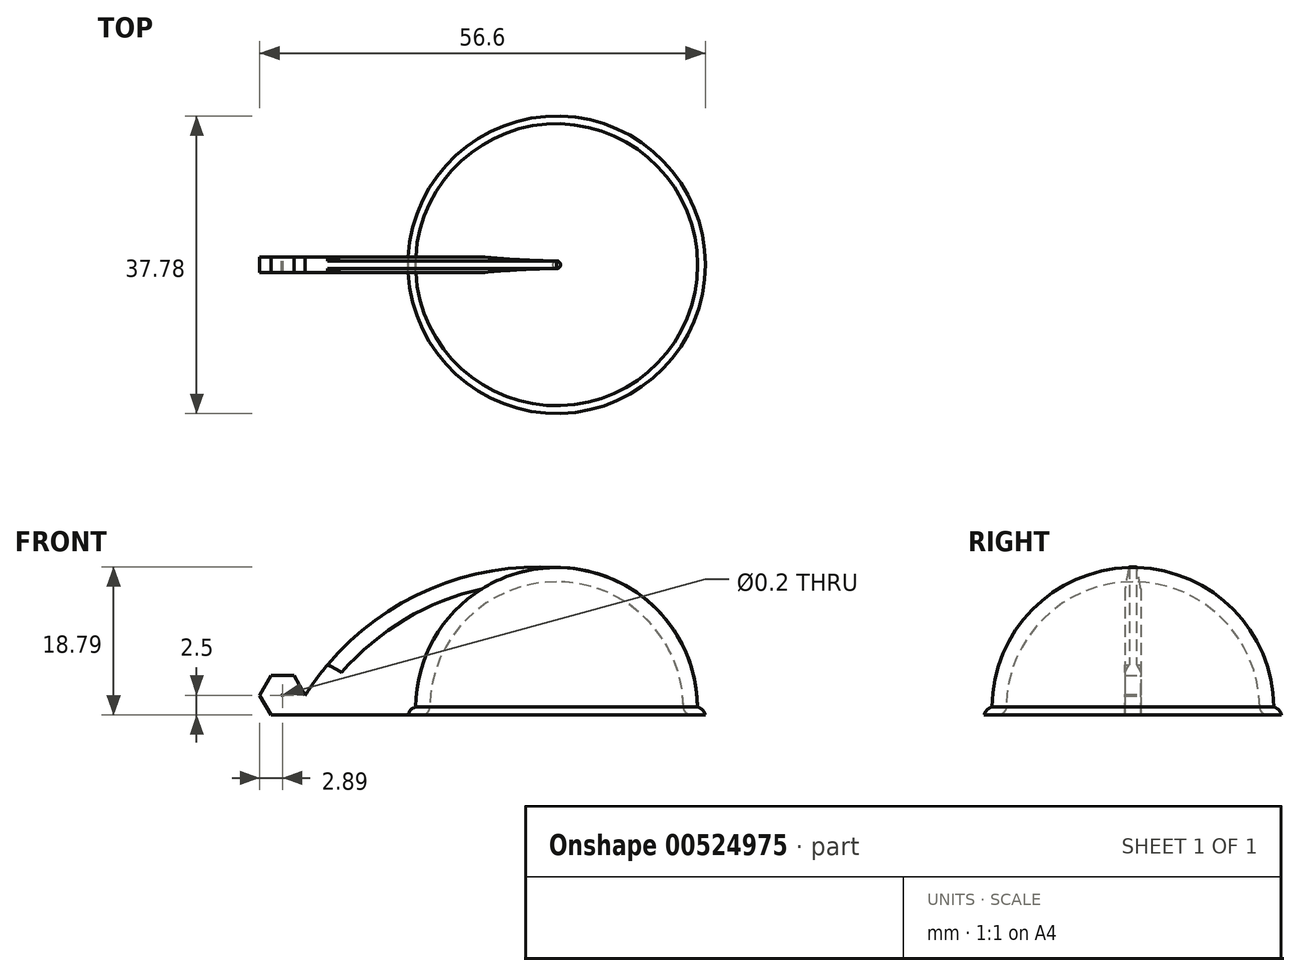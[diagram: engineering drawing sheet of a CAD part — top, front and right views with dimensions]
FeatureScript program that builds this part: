
annotation { "Feature Type Name" : "Feature", "Feature Type Description" : "" }
export const myFeature = defineFeature(function(context is Context, id is Id, definition is map)
    precondition{}
    {
        {
            var Q0;
            Q0=qCreatedBy(makeId("Front.planeOp"),FACE);
            var sketch = newSketch(context, id + "F0", { "sketchPlane" : qUnion([Q0])});
            skLineSegment(sketch, "E0", {"start": v(0, 0) * mm, "end": v(0, 0) * mm});
            skCircle(sketch, "E1.cCircle", {"center": v(0, 0) * mm, "radius": 2.89 * mm, "construction": true});
            skLineSegment(sketch, "E1.0", {"start": v(-1.44, 2.5) * mm, "end": v(1.44, 2.5) * mm});
            skLineSegment(sketch, "E1.1", {"start": v(1.44, 2.5) * mm, "end": v(2.89, 0) * mm});
            skLineSegment(sketch, "E1.3", {"start": v(1.44, -2.5) * mm, "end": v(-1.44, -2.5) * mm});
            skLineSegment(sketch, "E1.4", {"start": v(-1.44, -2.5) * mm, "end": v(-2.89, 0) * mm});
            skLineSegment(sketch, "E1.5", {"start": v(-2.89, 0) * mm, "end": v(-1.44, 2.5) * mm});
            skLineSegment(sketch, "E2", {"start": v(-17.6, 2.5) * mm, "end": v(3.84, 2.5) * mm, "construction": true});
            skArc(sketch, "E3", {"start": v(34.82, 16.21) * mm, "mid": v(22.22, 11.04) * mm, "end": v(16.9, -1.5) * mm});
            skLineSegment(sketch, "E4", {"start": v(15.92, -2.5) * mm, "end": v(12.44, -2.5) * mm});
            skLineSegment(sketch, "E5", {"start": v(1.44, -2.5) * mm, "end": v(12.44, -2.5) * mm});
            skArc(sketch, "E6", {"start": v(34.82, 16.21) * mm, "mid": v(16.62, 12.5) * mm, "end": v(2.89, 0) * mm});
            skLineSegment(sketch, "E7", {"start": v(-10.18, -3.59) * mm, "end": v(-10.18, 16.21) * mm, "construction": true});
            skLineSegment(sketch, "E8", {"start": v(-2.89, 0) * mm, "end": v(2.89, 0) * mm, "construction": true});
            skArc(sketch, "E9.0", {"start": v(34.82, 14.41) * mm, "mid": v(23.14, 9.4) * mm, "end": v(18.72, -2.5) * mm});
            skLineSegment(sketch, "E10", {"start": v(34.82, 14.41) * mm, "end": v(34.82, 16.21) * mm});
            skLineSegment(sketch, "E11", {"start": v(18.72, -2.5) * mm, "end": v(16.92, -2.5) * mm});
            skLineSegment(sketch, "E12", {"start": v(34.82, 16.21) * mm, "end": v(34.82, -2.5) * mm, "construction": true});
            skLineSegment(sketch, "E13", {"start": v(-1.44, -2.5) * mm, "end": v(-1.44, -6.64) * mm, "construction": true});
            skArc(sketch, "E14", {"start": v(12.44, -2.5) * mm, "mid": v(9.62, 1.25) * mm, "end": v(5.71, 3.86) * mm});
            skArc(sketch, "E15", {"start": v(16.9, -1.5) * mm, "mid": v(16.3, -1.88) * mm, "end": v(15.92, -2.5) * mm});
            skLineSegment(sketch, "E16", {"start": v(15.92, -2.5) * mm, "end": v(16.92, -2.5) * mm});
            skLineSegment(sketch, "E17", {"start": v(-5.18, -2.5) * mm, "end": v(34.82, -2.5) * mm, "construction": true});
            skLineSegment(sketch, "E18", {"start": v(0, 5.36) * mm, "end": v(0, -8.93) * mm, "construction": true});
            skLineSegment(sketch, "E19", {"start": v(34.32, 16.24) * mm, "end": v(34.32, 15) * mm});
            skLineSegment(sketch, "E20", {"start": v(34.32, 15) * mm, "end": v(34.82, 15) * mm});
            skLineSegment(sketch, "E21", {"start": v(34.82, 15) * mm, "end": v(34.82, 16.21) * mm});
            skCircle(sketch, "E22", {"center": v(0, 0) * mm, "radius": 0.1 * mm});
            skSolve(sketch);
        }
        {
            var Q0;
            Q0=makeQuery(id+"F0.imprint","IMPRINT",FACE,{"disambiguationData":[TD([[makeQuery(id+"F0.imprint","IMPRINT",EDGE,{"derivedFrom":sQuery(id+"F0.wireOp",EDGE,"E9.0")}),-1.0]])]});
            var Q1;
            Q1=sQuery(id+"F0.wireOp",EDGE,"E12");
            revolve(context, id + "F1", {"entities" : qUnion([Q0]), "axis" : qUnion([Q1]), "revolveType" : RevolveType.FULL});
        }
        {
            var Q0;
            {var subQ2=sQuery(id+"F0.wireOp",EDGE,"E3");Q0=makeQuery(id+"F0.imprint","IMPRINT",FACE,{"disambiguationData":[TD([[makeQuery(id+"F0.imprint","IMPRINT",EDGE,{"derivedFrom":subQ2}),-1.0]])]});}
            var Q1;
            Q1=makeQuery(id+"F0.imprint","IMPRINT",FACE,{"disambiguationData":[TD([[makeQuery(id+"F0.imprint","IMPRINT",EDGE,{"derivedFrom":sQuery(id+"F0.wireOp",EDGE,"E4")}),-1.0]])]});
            extrude(context, id + "F2", {"entities" : qUnion([Q0, Q1]), "operationType" : NewBodyOperationType.ADD, "depth" : 2 * mm, "offsetDistance" : 25 * mm, "symmetric" : true});
        }
        {
            var Q0;
            Q0=makeQuery(id+"F2.opExtrude","CAP_EDGE",EDGE,{"disambiguationData":[OSD([sQuery(id+"F0.wireOp",EDGE,"E6")])],"isStart":false});
            var Q1;
            Q1=makeQuery(id+"F2.opExtrude","CAP_EDGE",EDGE,{"disambiguationData":[OSD([sQuery(id+"F0.wireOp",EDGE,"E6")])],"isStart":true});
            chamfer(context, id + "F3", {"entities" : qUnion([Q0, Q1]), "chamferType" : ChamferType.OFFSET_ANGLE, "width" : 2 * mm, "oppositeDirection" : false, "angle" : 15 * degree, "tangentPropagation" : true});
        }
        {
            var Q0;
            Q0=makeQuery(id+"F0.imprint","IMPRINT",FACE,{"disambiguationData":[TD([[makeQuery(id+"F0.imprint","IMPRINT",EDGE,{"derivedFrom":sQuery(id+"F0.wireOp",EDGE,"E1.0")}),-1.0]])]});
            extrude(context, id + "F4", {"entities" : qUnion([Q0]), "operationType" : NewBodyOperationType.ADD, "depth" : 2 * mm, "offsetDistance" : 25 * mm, "symmetric" : true});
        }
        {
            var Q0;
            Q0=makeQuery(id+"F1.opRevolve","SWEPT_EDGE",EDGE,{"disambiguationData":[OSD([sQuery(id+"F0.wireOp",EDGE,"E9.0"),sQuery(id+"F0.wireOp",EDGE,"E11")])]});
            fillet(context, id + "F5", {"entities" : qUnion([Q0]), "radius" : 1 * mm, "tangentPropagation" : true, "allowEdgeOverflow" : false});
        }
        {
            var Q0;
            Q0=makeQuery(id+"F1.opRevolve","SWEPT_FACE",FACE,{"disambiguationData":[OSD([sQuery(id+"F0.wireOp",EDGE,"E20")])]});
            var sketch = newSketch(context, id + "F6", { "sketchPlane" : qUnion([Q0])});
            skCircle(sketch, "E23.0", {"center": v(34.82, 0) * mm, "radius": 0.5 * mm});
            skSolve(sketch);
        }
        {
            var Q0;
            Q0=makeQuery(id+"F6.imprint","IMPRINT",FACE,{"disambiguationData":[TD([[makeQuery(id+"F6.imprint","IMPRINT",EDGE,{"derivedFrom":sQuery(id+"F6.wireOp",EDGE,"E23.0")}),1.0]])]});
            var Q1;
            Q1=makeQuery(id+"F2.opExtrude","SWEPT_BODY",BODY,{"disambiguationData":[OSD([sQuery(id+"F0.wireOp",EDGE,"E3"),sQuery(id+"F0.wireOp",EDGE,"E4"),sQuery(id+"F0.wireOp",EDGE,"E6"),sQuery(id+"F0.wireOp",EDGE,"E14"),sQuery(id+"F0.wireOp",EDGE,"E15")])]});
            extrude(context, id + "F7", {"entities" : qUnion([Q0]), "operationType" : NewBodyOperationType.ADD, "depth" : 1.2 * mm, "endBoundEntityBody" : qUnion([Q1]), "offsetDistance" : 25 * mm});
        }
    });
